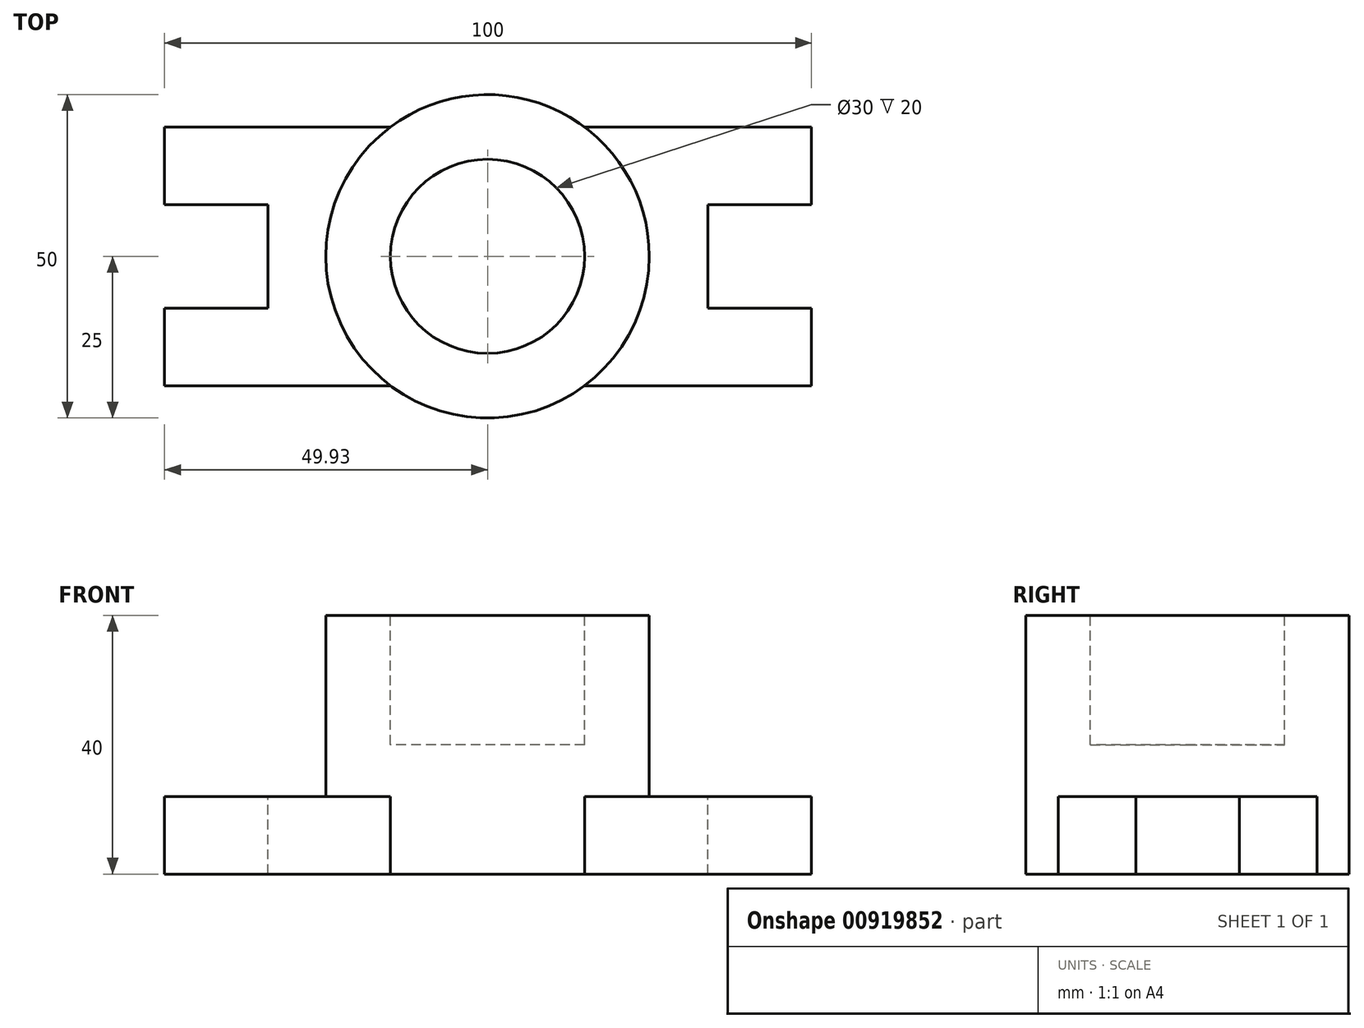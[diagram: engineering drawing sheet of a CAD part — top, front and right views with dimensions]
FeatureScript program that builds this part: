
annotation { "Feature Type Name" : "Feature", "Feature Type Description" : "" }
export const myFeature = defineFeature(function(context is Context, id is Id, definition is map)
    precondition{}
    {
        {
            var Q0;
            Q0=qCreatedBy(makeId("Top.planeOp"),FACE);
            var sketch = newSketch(context, id + "F0", { "sketchPlane" : qUnion([Q0])});
            skCircle(sketch, "E0", {"center": v(0, 0) * mm, "radius": 25 * mm});
            skSolve(sketch);
        }
        {
            var Q0;
            Q0=makeQuery(id+"F0.imprint","IMPRINT",FACE,{"disambiguationData":[TD([[makeQuery(id+"F0.imprint","IMPRINT",EDGE,{"derivedFrom":sQuery(id+"F0.wireOp",EDGE,"E0")}),1.0]])]});
            extrude(context, id + "F1", {"entities" : qUnion([Q0]), "depth" : 40 * mm, "offsetDistance" : 25.4 * mm});
        }
        {
            var Q0;
            Q0=makeQuery(id+"F1.opExtrude","CAP_FACE",FACE,{"disambiguationData":[OSD([sQuery(id+"F0.wireOp",EDGE,"E0")])],"isStart":false});
            var sketch = newSketch(context, id + "F2", { "sketchPlane" : qUnion([Q0])});
            skCircle(sketch, "E1", {"center": v(0, 0) * mm, "radius": 15 * mm});
            skSolve(sketch);
        }
        {
            var Q0;
            Q0=makeQuery(id+"F2.imprint","IMPRINT",FACE,{"disambiguationData":[TD([[makeQuery(id+"F2.imprint","IMPRINT",EDGE,{"derivedFrom":sQuery(id+"F2.wireOp",EDGE,"E1")}),1.0]])]});
            extrude(context, id + "F3", {"entities" : qUnion([Q0]), "operationType" : NewBodyOperationType.REMOVE, "oppositeDirection" : true, "depth" : 20 * mm, "offsetDistance" : 25.4 * mm});
        }
        {
            var Q0;
            Q0=makeQuery(id+"F1.opExtrude","CAP_FACE",FACE,{"disambiguationData":[OSD([sQuery(id+"F0.wireOp",EDGE,"E0")])],"isStart":true});
            var sketch = newSketch(context, id + "F4", { "sketchPlane" : qUnion([Q0])});
            skLineSegment(sketch, "E2.bottom", {"start": v(-49.93, 20) * mm, "end": v(50.07, 20) * mm});
            skLineSegment(sketch, "E2.top", {"start": v(-49.93, -20) * mm, "end": v(50.07, -20) * mm});
            skLineSegment(sketch, "E2.left", {"start": v(-49.93, 20) * mm, "end": v(-49.93, -20) * mm});
            skLineSegment(sketch, "E2.right", {"start": v(50.07, 20) * mm, "end": v(50.07, -20) * mm});
            skSolve(sketch);
        }
        {
            var Q0;
            {var subQ0=sQuery(id+"F4.wireOp",EDGE,"E2.right");Q0=makeQuery(id+"F4.imprint","IMPRINT",FACE,{"disambiguationData":[TD([[makeQuery(id+"F4.imprint","IMPRINT",EDGE,{"derivedFrom":subQ0}),-1.0]])]});}
            var Q1;
            {var subQ0=sQuery(id+"F4.wireOp",EDGE,"E2.left");Q1=makeQuery(id+"F4.imprint","IMPRINT",FACE,{"disambiguationData":[TD([[makeQuery(id+"F4.imprint","IMPRINT",EDGE,{"derivedFrom":subQ0}),1.0]])]});}
            var Q2;
            {var subQ0=sQuery(id+"F4.wireOp",EDGE,"E2.bottom");var subQ1=makeQuery(id+"F1.opExtrude","CAP_EDGE",EDGE,{"disambiguationData":[OSD([sQuery(id+"F0.wireOp",EDGE,"E0")])],"isStart":true});var subQ2=makeQuery(id+"F4.imprint","INTERSECT",VERTEX,{"disambiguationData":[OD(0.0)],"derivedFrom":[subQ1,subQ0]});Q2=makeQuery(id+"F4.imprint","IMPRINT",FACE,{"disambiguationData":[TD([[makeQuery(id+"F4.imprint","IMPRINT",EDGE,{"disambiguationData":[TD([[subQ2,-1.0]])],"derivedFrom":subQ0}),-1.0]])]});}
            extrude(context, id + "F5", {"entities" : qUnion([Q0, Q1, Q2]), "operationType" : NewBodyOperationType.ADD, "oppositeDirection" : true, "depth" : 12 * mm, "offsetDistance" : 25.4 * mm});
        }
        {
            var Q0;
            {var subQ0=sQuery(id+"F4.wireOp",EDGE,"E2.top");var subQ1=sQuery(id+"F4.wireOp",EDGE,"E2.bottom");var subQ2=sQuery(id+"F4.wireOp",EDGE,"E2.left");Q0=makeQuery(id+"F5.boolean.opBoolean","SPLIT",FACE,{"disambiguationData":[TD([makeQuery(id+"F5.opExtrude","SWEPT_FACE",FACE,{"disambiguationData":[OSD([subQ2])]})])],"derivedFrom":makeQuery(id+"F5.opExtrude","CAP_FACE",FACE,{"disambiguationData":[OSD([subQ1,subQ0,subQ2,sQuery(id+"F4.wireOp",EDGE,"E2.right")])],"isStart":false})});}
            var sketch = newSketch(context, id + "F6", { "sketchPlane" : qUnion([Q0])});
            skLineSegment(sketch, "E3", {"start": v(-49.93, 8) * mm, "end": v(-33.93, 8) * mm});
            skLineSegment(sketch, "E4", {"start": v(-33.93, 8) * mm, "end": v(-33.93, -8) * mm});
            skLineSegment(sketch, "E5", {"start": v(-33.93, -8) * mm, "end": v(-49.93, -8) * mm});
            skSolve(sketch);
        }
        {
            var Q0;
            {var subQ0=sQuery(id+"F6.wireOp",EDGE,"E3");Q0=makeQuery(id+"F6.imprint","IMPRINT",FACE,{"disambiguationData":[TD([[makeQuery(id+"F6.imprint","IMPRINT",EDGE,{"derivedFrom":subQ0}),-1.0]])]});}
            extrude(context, id + "F7", {"entities" : qUnion([Q0]), "operationType" : NewBodyOperationType.REMOVE, "oppositeDirection" : true, "depth" : 12 * mm, "offsetDistance" : 25.4 * mm});
        }
        {
            var Q0;
            {var subQ0=sQuery(id+"F4.wireOp",EDGE,"E2.top");var subQ1=sQuery(id+"F4.wireOp",EDGE,"E2.bottom");var subQ2=sQuery(id+"F4.wireOp",EDGE,"E2.right");Q0=makeQuery(id+"F5.boolean.opBoolean","SPLIT",FACE,{"disambiguationData":[TD([makeQuery(id+"F5.opExtrude","SWEPT_FACE",FACE,{"disambiguationData":[OSD([subQ2])]})])],"derivedFrom":makeQuery(id+"F5.opExtrude","CAP_FACE",FACE,{"disambiguationData":[OSD([subQ1,subQ0,sQuery(id+"F4.wireOp",EDGE,"E2.left"),subQ2])],"isStart":false})});}
            var sketch = newSketch(context, id + "F8", { "sketchPlane" : qUnion([Q0])});
            skLineSegment(sketch, "E6.bottom", {"start": v(50.07, 8) * mm, "end": v(34.07, 8) * mm});
            skLineSegment(sketch, "E6.top", {"start": v(50.07, -8) * mm, "end": v(34.07, -8) * mm});
            skLineSegment(sketch, "E6.left", {"start": v(50.07, 8) * mm, "end": v(50.07, -8) * mm});
            skLineSegment(sketch, "E6.right", {"start": v(34.07, 8) * mm, "end": v(34.07, -8) * mm});
            skSolve(sketch);
        }
        {
            var Q0;
            Q0=makeQuery(id+"F8.imprint","IMPRINT",FACE,{"disambiguationData":[TD([[makeQuery(id+"F8.imprint","IMPRINT",EDGE,{"derivedFrom":sQuery(id+"F8.wireOp",EDGE,"E6.bottom")}),1.0]])]});
            extrude(context, id + "F9", {"entities" : qUnion([Q0]), "operationType" : NewBodyOperationType.REMOVE, "oppositeDirection" : true, "depth" : 12 * mm, "offsetDistance" : 25.4 * mm});
        }
    });
